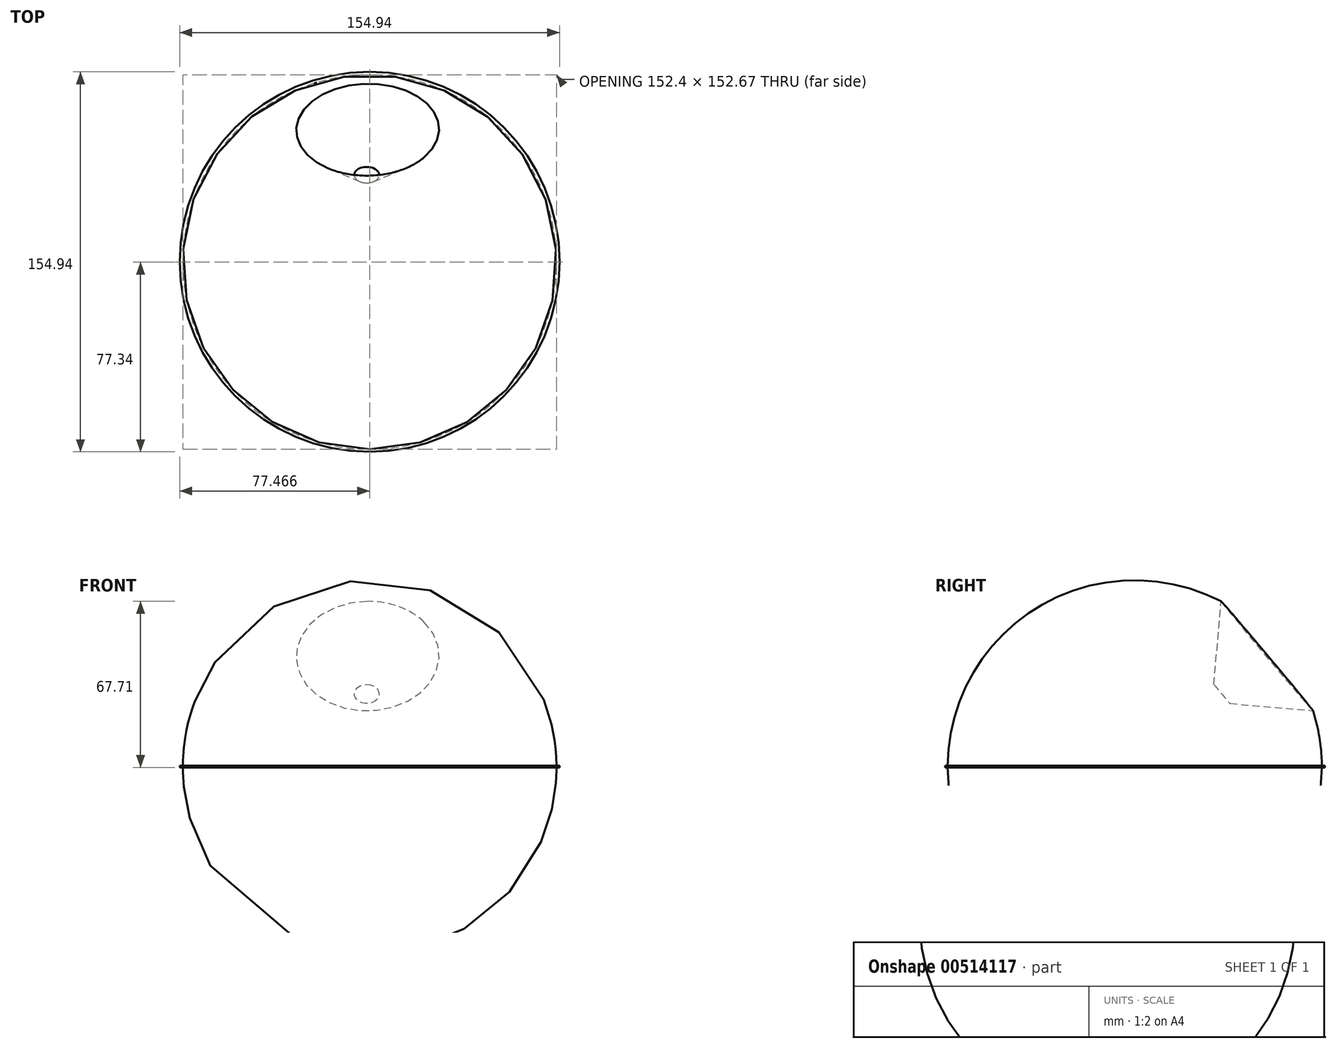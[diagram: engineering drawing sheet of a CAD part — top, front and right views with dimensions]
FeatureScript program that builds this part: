
annotation { "Feature Type Name" : "Feature", "Feature Type Description" : "" }
export const myFeature = defineFeature(function(context is Context, id is Id, definition is map)
    precondition{}
    {
        {
            var Q0;
            Q0=qCreatedBy(makeId("Top.planeOp"),FACE);
            var sketch = newSketch(context, id + "F0", { "sketchPlane" : qUnion([Q0])});
            skLineSegment(sketch, "E0.bottom", {"start": v(-74.92, 76.48) * mm, "end": v(77.48, 76.48) * mm, "construction": true});
            skLineSegment(sketch, "E0.top", {"start": v(-74.92, -75.92) * mm, "end": v(77.48, -75.92) * mm, "construction": true});
            skLineSegment(sketch, "E0.left", {"start": v(-74.92, 76.48) * mm, "end": v(-74.92, -75.92) * mm, "construction": true});
            skLineSegment(sketch, "E0.right", {"start": v(77.48, 76.48) * mm, "end": v(77.48, -75.92) * mm, "construction": true});
            skLineSegment(sketch, "E1", {"start": v(1.28, 76.48) * mm, "end": v(0, -75.92) * mm, "construction": true});
            skPoint(sketch, "E1.endSnap0", {"position": v(1.28, -75.92) * mm});
            skArc(sketch, "E2", {"start": v(77.48, 0) * mm, "mid": v(1.42, 76.48) * mm, "end": v(-74.92, 0.28) * mm});
            skLineSegment(sketch, "E3", {"start": v(-74.92, 0.28) * mm, "end": v(77.48, 0) * mm});
            skSolve(sketch);
        }
        {
            var Q0;
            Q0 = qSketchRegion(id + "F0", true);
            var Q1;
            Q1=sQuery(id+"F0.wireOp",EDGE,"E2");
            var Q2;
            Q2=sQuery(id+"F0.wireOp",EDGE,"E3");
            revolve(context, id + "F1", {"entities" : qUnion([Q0]), "surfaceEntities" : qUnion([Q1]), "axis" : qUnion([Q2]), "revolveType" : RevolveType.FULL});
        }
        {
            var Q0;
            Q0=qCreatedBy(makeId("Top.planeOp"),FACE);
            var Q1;
            Q1=makeQuery(id+"F1.opRevolve","SWEPT_FACE",FACE,{"disambiguationData":[OSD([sQuery(id+"F0.wireOp",EDGE,"E2")])]});
            cPlane(context, id + "F2", {"entities" : qUnion([Q0, Q1]), "cplaneType" : CPlaneType.LINE_ANGLE, "offset" : 60.7 * mm, "angle" : 130 * degree, "oppositeDirection" : true, "width" : 152.4 * mm, "height" : 152.4 * mm});
        }
        {
            var Q0;
            Q0=qCreatedBy(id+"F2.planeOp",FACE);
            cPlane(context, id + "F3", {"entities" : qUnion([Q0]), "cplaneType" : CPlaneType.OFFSET, "offset" : 109.98 * mm, "width" : 152.4 * mm, "height" : 152.4 * mm});
        }
        {
            var Q0;
            Q0=qCreatedBy(id+"F3.planeOp",FACE);
            var sketch = newSketch(context, id + "F4", { "sketchPlane" : qUnion([Q0])});
            skCircle(sketch, "E4", {"center": v(0, 0) * mm, "radius": 50.8 * mm});
            skSolve(sketch);
        }
        {
            var Q0;
            Q0=makeQuery(id+"F4.imprint","IMPRINT",FACE,{"disambiguationData":[TD([[makeQuery(id+"F4.imprint","IMPRINT",EDGE,{"derivedFrom":sQuery(id+"F4.wireOp",EDGE,"E4")}),1.0]])]});
            extrude(context, id + "F5", {"entities" : qUnion([Q0]), "operationType" : NewBodyOperationType.REMOVE, "oppositeDirection" : true, "depth" : 63.5 * mm, "offsetDistance" : 25.4 * mm});
        }
        {
            var Q0;
            Q0=makeQuery(id+"F5.boolean.opBoolean","COPY",EDGE,{"derivedFrom":makeQuery(id+"F5.opExtrude","CAP_EDGE",EDGE,{"disambiguationData":[OSD([sQuery(id+"F4.wireOp",EDGE,"E4")])],"isStart":false})});
            chamfer(context, id + "F6", {"entities" : qUnion([Q0]), "width" : 45.72 * mm, "tangentPropagation" : true});
        }
        {
            var Q0;
            Q0=qCreatedBy(makeId("Top.planeOp"),FACE);
            var sketch = newSketch(context, id + "F7", { "sketchPlane" : qUnion([Q0])});
            skCircle(sketch, "E5", {"center": v(1.28, 0.27) * mm, "radius": 77.47 * mm});
            skSolve(sketch);
        }
        {
            var Q0;
            Q0 = qSketchRegion(id + "F7", true);
            extrude(context, id + "F8", {"entities" : qUnion([Q0]), "operationType" : NewBodyOperationType.ADD, "depth" : 0.76 * mm, "offsetDistance" : 25.4 * mm});
        }
    });
